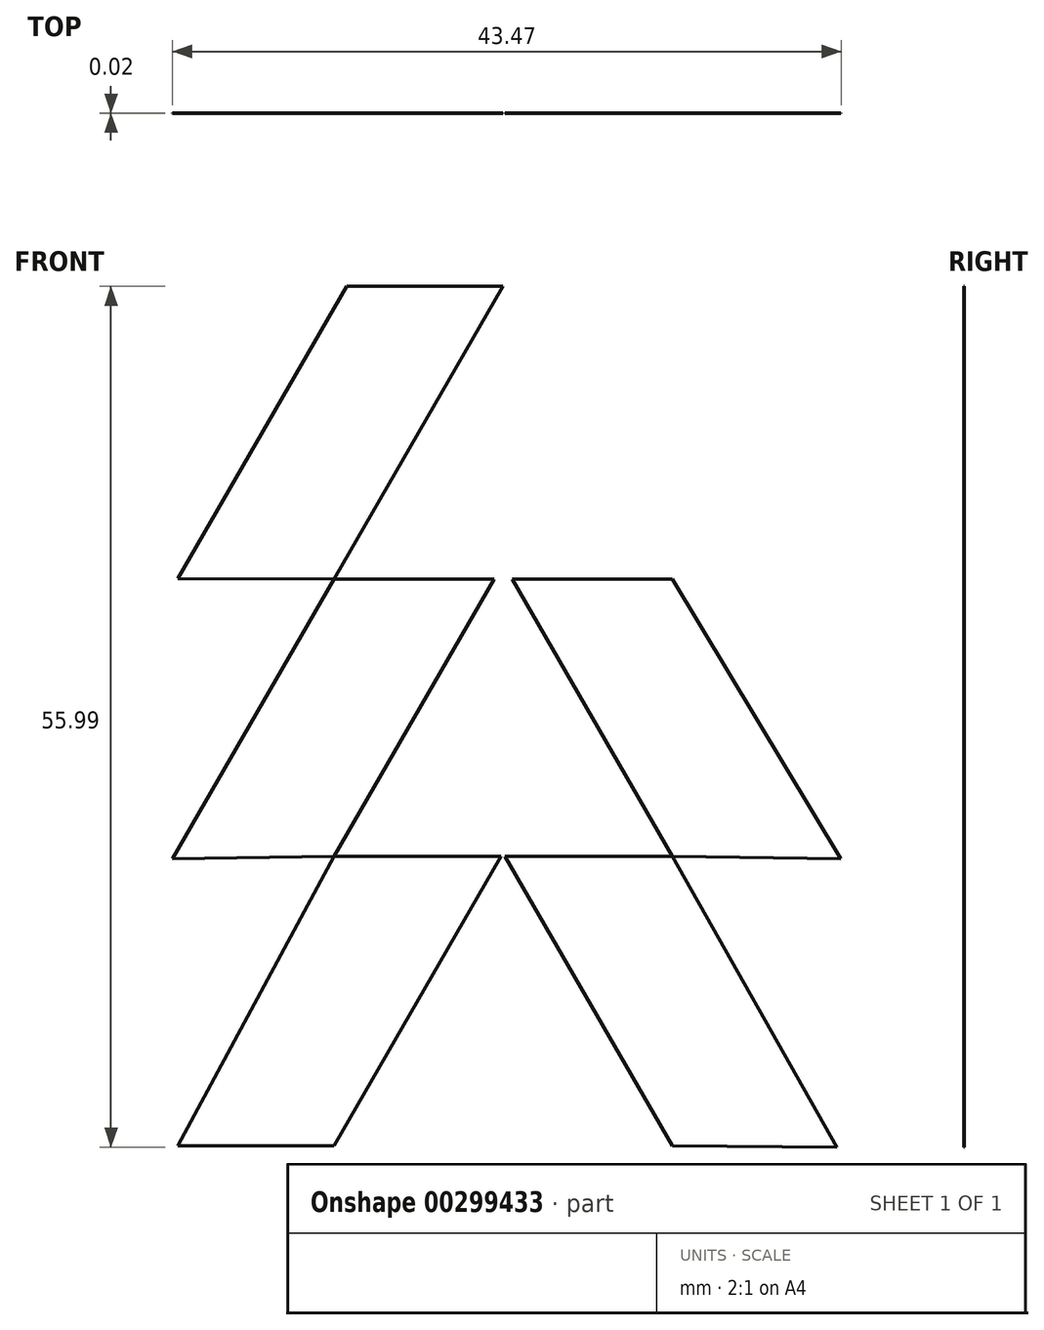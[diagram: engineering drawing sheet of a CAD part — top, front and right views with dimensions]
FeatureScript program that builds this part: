
annotation { "Feature Type Name" : "Feature", "Feature Type Description" : "" }
export const myFeature = defineFeature(function(context is Context, id is Id, definition is map)
    precondition{}
    {
        {
            var Q0;
            Q0=qCreatedBy(makeId("Front.planeOp"),FACE);
            var sketch = newSketch(context, id + "F0", { "sketchPlane" : qUnion([Q0])});
            skCircle(sketch, "E0.cCircle", {"center": v(0, 0) * mm, "radius": 12.7 * mm, "construction": true});
            skLineSegment(sketch, "E0.0", {"start": v(0, 12.7) * mm, "end": v(11, -6.35) * mm});
            skLineSegment(sketch, "E0.1", {"start": v(11, -6.35) * mm, "end": v(-11, -6.35) * mm});
            skLineSegment(sketch, "E0.2", {"start": v(-11, -6.35) * mm, "end": v(0, 12.7) * mm});
            skLineSegment(sketch, "E1", {"start": v(0, 12.7) * mm, "end": v(-10.16, 12.7) * mm});
            skLineSegment(sketch, "E2", {"start": v(-10.16, 12.7) * mm, "end": v(-21.16, -6.3) * mm});
            skLineSegment(sketch, "E3", {"start": v(-21.16, -6.3) * mm, "end": v(-11, -6.35) * mm});
            skLineSegment(sketch, "E4.MirrorCS", {"start": v(11, -6.35) * mm, "end": v(0, 12.7) * mm});
            skLineSegment(sketch, "E5.MirrorCS", {"start": v(0, 12.7) * mm, "end": v(10.16, 12.7) * mm});
            skLineSegment(sketch, "E6.MirrorCS", {"start": v(10.16, 12.7) * mm, "end": v(21.16, -6.3) * mm});
            skLineSegment(sketch, "E7.MirrorCS", {"start": v(21.16, -6.3) * mm, "end": v(11, -6.35) * mm});
            skCircle(sketch, "E8.cCircle", {"center": v(0, -18.04) * mm, "radius": 12.7 * mm, "construction": true});
            skPoint(sketch, "E8.cCircle.centerSnap0", {"position": v(0, -6.35) * mm});
            skLineSegment(sketch, "E8.0", {"start": v(11, -24.39) * mm, "end": v(-11, -24.39) * mm});
            skLineSegment(sketch, "E8.1", {"start": v(-11, -24.39) * mm, "end": v(0, -5.34) * mm});
            skLineSegment(sketch, "E8.2", {"start": v(0, -5.34) * mm, "end": v(11, -24.39) * mm});
            skLineSegment(sketch, "E9", {"start": v(11, -6.35) * mm, "end": v(21.98, -24.53) * mm});
            skLineSegment(sketch, "E10", {"start": v(21.98, -24.53) * mm, "end": v(11, -24.39) * mm});
            skLineSegment(sketch, "E11", {"start": v(-11, -6.35) * mm, "end": v(-21.5, -24.53) * mm});
            skLineSegment(sketch, "E12", {"start": v(-21.5, -24.53) * mm, "end": v(-11, -24.39) * mm});
            skCircle(sketch, "E13.cCircle", {"center": v(0, -36.86) * mm, "radius": 12.7 * mm, "construction": true});
            skLineSegment(sketch, "E13.0", {"start": v(11, -43.2) * mm, "end": v(-11, -43.2) * mm});
            skLineSegment(sketch, "E13.1", {"start": v(-11, -43.2) * mm, "end": v(0, -24.16) * mm});
            skLineSegment(sketch, "E13.2", {"start": v(0, -24.16) * mm, "end": v(11, -43.2) * mm});
            skLineSegment(sketch, "E14", {"start": v(11, -24.39) * mm, "end": v(21.71, -43.29) * mm});
            skLineSegment(sketch, "E15", {"start": v(21.71, -43.29) * mm, "end": v(11, -43.2) * mm});
            skLineSegment(sketch, "E16", {"start": v(-11, -24.39) * mm, "end": v(-21.16, -43.2) * mm});
            skLineSegment(sketch, "E17", {"start": v(-21.16, -43.2) * mm, "end": v(-11, -43.2) * mm});
            skSolve(sketch);
        }
        {
            var Q0;
            Q0=makeQuery(id+"F0.imprint","IMPRINT",FACE,{"disambiguationData":[TD([[makeQuery(id+"F0.imprint","IMPRINT",EDGE,{"derivedFrom":sQuery(id+"F0.wireOp",EDGE,"E0.2")}),1.0]])]});
            var Q1;
            Q1=makeQuery(id+"F0.imprint","IMPRINT",FACE,{"disambiguationData":[TD([[makeQuery(id+"F0.imprint","IMPRINT",EDGE,{"derivedFrom":sQuery(id+"F0.wireOp",EDGE,"E4.MirrorCS")}),-1.0]])]});
            var Q2;
            {var subQ0=sQuery(id+"F0.wireOp",EDGE,"E11");Q2=makeQuery(id+"F0.imprint","IMPRINT",FACE,{"disambiguationData":[TD([[makeQuery(id+"F0.imprint","IMPRINT",EDGE,{"derivedFrom":subQ0}),1.0]])]});}
            var Q3;
            {var subQ0=sQuery(id+"F0.wireOp",EDGE,"E9");Q3=makeQuery(id+"F0.imprint","IMPRINT",FACE,{"disambiguationData":[TD([[makeQuery(id+"F0.imprint","IMPRINT",EDGE,{"derivedFrom":subQ0}),-1.0]])]});}
            var Q4;
            {var subQ0=sQuery(id+"F0.wireOp",EDGE,"E16");Q4=makeQuery(id+"F0.imprint","IMPRINT",FACE,{"disambiguationData":[TD([[makeQuery(id+"F0.imprint","IMPRINT",EDGE,{"derivedFrom":subQ0}),1.0]])]});}
            var Q5;
            {var subQ0=sQuery(id+"F0.wireOp",EDGE,"E14");Q5=makeQuery(id+"F0.imprint","IMPRINT",FACE,{"disambiguationData":[TD([[makeQuery(id+"F0.imprint","IMPRINT",EDGE,{"derivedFrom":subQ0}),-1.0]])]});}
            extrude(context, id + "F1", {"entities" : qUnion([Q0, Q1, Q2, Q3, Q4, Q5]), "depth" : 1 / 50.8 * mm});
        }
    });
